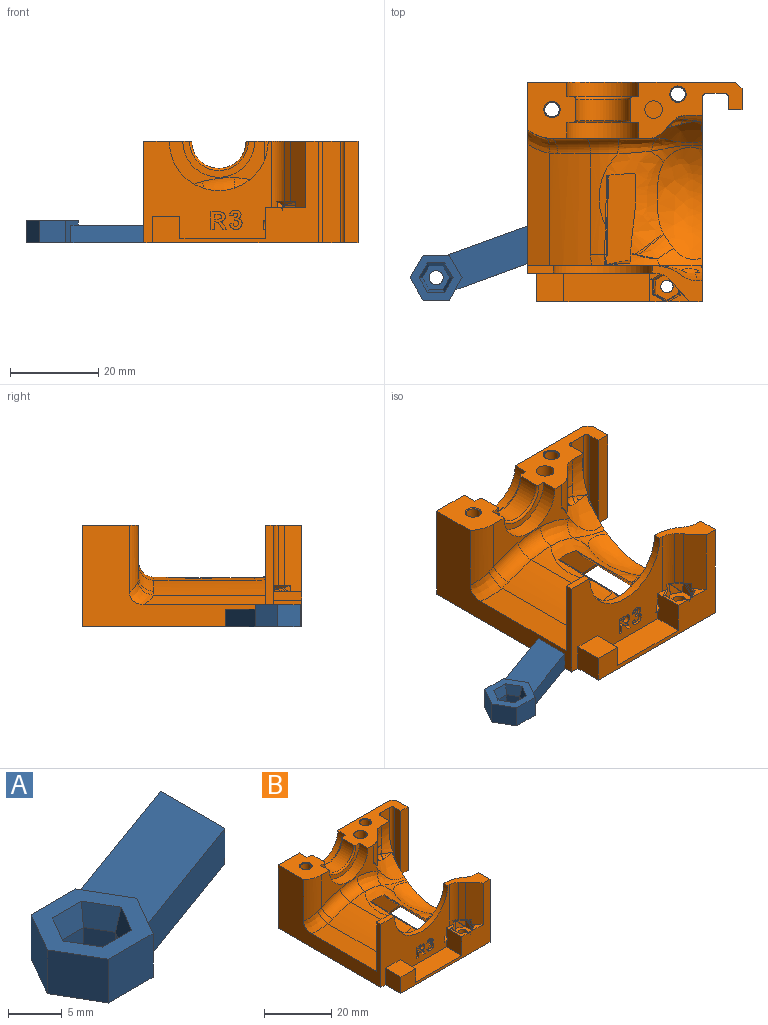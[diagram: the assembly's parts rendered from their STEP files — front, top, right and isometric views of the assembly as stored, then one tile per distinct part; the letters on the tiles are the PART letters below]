
ASSEMBLY  parts=2 mates=1
PART A: 26 faces, bbox 26.7x16.8x5 mm
  f0: plane 2.68x1.9mm, normal (0.87,-0.5,0), area 5.9mm2, adj f1,f5,f8,f12
  f1: plane 3.1x1.9mm, normal (0,-1,0), area 5.9mm2, adj f0,f2,f7,f12
  f2: plane 2.68x1.9mm, normal (-0.87,-0.5,0), area 5.9mm2, adj f1,f3,f6,f12
  f3: plane 2.68x1.9mm, normal (-0.87,0.5,0), area 5.9mm2, adj f2,f4,f11,f12
  f4: plane 3.1x1.9mm, normal (0,1,0), area 5.9mm2, adj f3,f5,f10,f12
  f5: plane 2.68x1.9mm, normal (0.87,0.5,0), area 5.9mm2, adj f0,f4,f9,f12
  f6: plane 3.33x2.5mm, normal (-0.84,-0.48,0.25), area 9mm2, adj f2,f7,f11,f13
  f7: plane 3.85x2.5mm, normal (0,-0.97,0.25), area 9mm2, adj f1,f6,f8,f13
  f8: plane 3.33x2.5mm, normal (0.84,-0.48,0.25), area 9mm2, adj f0,f7,f9,f13
  f9: plane 3.33x2.5mm, normal (0.84,0.48,0.25), area 9mm2, adj f5,f8,f10,f13
  f10: plane 3.85x2.5mm, normal (0,0.97,0.25), area 9mm2, adj f4,f9,f11,f13
  f11: plane 3.33x2.5mm, normal (-0.84,0.48,0.25), area 9mm2, adj f3,f6,f10,f13
  f12: plane 6.2x5.37mm, normal (0,0,1), area 16.9mm2, adj f0,f1,f2,f3,f4,f5,f17
  f13: plane 11.8x10.22mm, normal (0,0,1), area 51.9mm2, adj f6,f7,f8,f9,f10,f11,f14,f15
  f14: plane 5.11x5mm, normal (-0.87,0.5,0), area 29.5mm2, adj f13,f15,f19,f24
  f15: plane 5.11x5mm, normal (-0.87,-0.5,0), area 29.5mm2, adj f13,f14,f16,f24
  f16: plane 5.9x5mm, normal (0,-1,0), area 29.5mm2, adj f13,f15,f20,f24
  f17: cylinder r=1.6mm len=3.2mm, axis (0,0,1), area 6mm2, adj f12,f24
  f18: plane 5.11x2.95mm, normal (0.87,0.5,0), area 5.9mm2, adj f13,f19,f20,f21
  f19: plane 5.9x5mm, normal (0,1,0), area 28.3mm2, adj f13,f14,f18,f21,f23,f24
  f20: plane 5.11x5mm, normal (0.87,-0.5,0), area 16.5mm2, adj f13,f16,f18,f21,f22,f24
  f21: plane 18.11x14.51mm, normal (0,0,1), area 137.7mm2, adj f18,f19,f20,f22,f23,f25
  f22: plane 16.47x6mm, normal (0.34,-0.94,0), area 70.1mm2, adj f20,f21,f24,f25
  f23: plane 18.11x6.59mm, normal (-0.34,0.94,0), area 77.1mm2, adj f19,f21,f24,f25
  f24: plane 26.65x16.81mm, normal (0,0,-1), area 220.1mm2, adj f14,f15,f16,f17,f19,f20,f22,f23
  f25: plane 8.51x4mm, normal (1,0,0), area 34.1mm2, adj f21,f22,f23,f24
PART B: 269 faces, bbox 50.7x51.1x25 mm
  f0: cone r=2.1mm half-angle=24.2deg, axis (0,0,-1), area 12.9mm2, adj f212,f229
  f1: cylinder r=3.1mm len=6.2mm, axis (0,0,-1), area 91.2mm2, adj f127,f129,f208,f209,f210,f211,f229
  f2: cylinder r=2mm len=9.54mm, axis (1,0.06,0), area 24.3mm2, adj f206,f207,f227,f228,f229
  f3: cone r=1.66mm half-angle=13.1deg, axis (0,0,-1), area 11.1mm2, adj f5,f229
  f4: cylinder r=3.1mm len=8mm, axis (0,0,1), area 76.4mm2, adj f105,f191,f192,f193,f194,f229
  f5: cylinder r=1.4mm len=4.71mm, axis (0,0,1), area 41.4mm2, adj f3,f121
  f6: cylinder r=8.15mm len=16.3mm, axis (0,-1,0), area 85.8mm2, adj f109,f195,f199,f224
  f7: cone r=1.6mm half-angle=45deg, axis (1,0,0), area 2.7mm2, adj f14,f216
  f8: cone r=1.6mm half-angle=45deg, axis (1,0,0), area 2.7mm2, adj f15,f216
  f9: cone r=1.85mm half-angle=45deg, axis (0,0,1), area 3.1mm2, adj f16,f199
  f10: cylinder r=8.15mm len=16.3mm, axis (0,-1,0), area 92.2mm2, adj f63,f114,f195,f199
  f11: cylinder r=6.15mm len=12.3mm, axis (0,-1,0), area 92.7mm2, adj f61,f62,f195,f199
  f12: cone r=1.85mm half-angle=45deg, axis (0,0,1), area 3.1mm2, adj f18,f195
  f13: cylinder r=2mm len=4mm, axis (0,0,1), area 50.3mm2, adj f59,f195
  f14: cylinder r=1.4mm len=12.3mm, axis (1,0,0), area 108.2mm2, adj f7,f57
  f15: cylinder r=1.4mm len=12.3mm, axis (1,0,0), area 106.9mm2, adj f8,f144,f182,f213
  f16: cylinder r=1.65mm len=17.3mm, axis (0,0,1), area 179.4mm2, adj f9,f83
  f17: cylinder r=1.65mm len=11.9mm, axis (0,0,1), area 123.4mm2, adj f28,f113
  f18: cylinder r=1.65mm len=14.3mm, axis (0,0,1), area 148.3mm2, adj f12,f58
  f19: plane 1.92x0.27mm, normal (0.04,-1,0), area 0.2mm2, adj f20,f21,f22,f25,f96
  f20: plane 0.08x0mm, normal (0,0,1), area 0mm2, adj f19,f25
  f21: plane 1.07x0.04mm, normal (-0.31,0.95,0), area 0mm2, adj f19,f22,f25
  f22: plane 0.91x0.27mm, normal (-0.52,0.84,-0.15), area 0mm2, adj f19,f21,f25
  f23: plane 1.69x0.97mm, normal (0,-1,0), area 1.5mm2, adj f37,f38,f39,f40,f41,f42
  f24: plane 1.79x0.78mm, normal (-1,0.01,0.06), area 0.6mm2, adj f36,f47,f48,f121
  f25: plane 2.08x0.62mm, normal (0,1,0), area 0.3mm2, adj f19,f20,f21,f22,f26,f50,f52,f94
  f26: plane 0.03x0.02mm, normal (0.49,-0.86,0.16), area 0mm2, adj f25,f50,f52
  f27: plane 4.08x3.33mm, normal (-0.18,-0.29,-0.94), area 3.6mm2, adj f34,f35,f43,f48,f53,f85,f86,f90
  f28: plane 3.3x3.3mm, normal (0,0,-1), area 8.6mm2, adj f17
  f29: plane 2.07x1.78mm, normal (-0.58,0.14,0.8), area 0.1mm2, adj f31,f51,f70,f121
  f30: plane 1.76x0.2mm, normal (0.62,0.78,0.09), area 0.2mm2, adj f45,f46,f70,f74
  f31: plane 2.45x1.78mm, normal (0.49,0.86,0.15), area 2.5mm2, adj f29,f51,f71
  f32: plane 2.66x0.44mm, normal (-0.13,-0.98,0.17), area 0mm2, adj f43,f72,f85
  f33: plane 2.67x2.57mm, normal (-0.34,-0.9,0.27), area 0.3mm2, adj f35,f72,f121
  f34: plane 3.23x2.92mm, normal (-1,0.01,0.04), area 1.4mm2, adj f27,f48,f73
  f35: plane 2.74x2.67mm, normal (-0.52,-0.85,0.06), area 4.3mm2, adj f27,f33,f73,f121
  f36: plane 1.69x0.17mm, normal (0.04,1,0.07), area 0.1mm2, adj f24,f46,f47,f74,f121
  f37: plane 0.65x0.2mm, normal (0,0,1), area 0.1mm2, adj f23,f38,f42,f84
  f38: extruded ~0.61x0.2mm, area 0.1mm2, adj f23,f37,f39,f84
  f39: extruded ~0.46x0.43mm, area 0.1mm2, adj f23,f38,f40,f84
  f40: extruded ~1.07x0.5mm, area 0.3mm2, adj f23,f39,f41,f84
  f41: plane 0.62x0.2mm, normal (0,0,-1), area 0.1mm2, adj f23,f40,f42,f84
  f42: plane 0.97x0.2mm, normal (-1,0,0), area 0.2mm2, adj f23,f37,f41,f84
  f43: plane 2.26x0.4mm, normal (-0.15,-0.97,0.17), area 0.2mm2, adj f27,f32,f85
  f44: plane 3.3x1.76mm, normal (0.97,0,0.24), area 3mm2, adj f49,f71,f85
  f45: plane 0.23x0.2mm, normal (0.59,0.81,0.04), area 0mm2, adj f30,f46,f51,f88
  f46: plane 2.96x1.71mm, normal (-0.45,0.78,0.42), area 0.6mm2, adj f30,f36,f45,f47,f74,f88,f89
  f47: plane 0.88x0.17mm, normal (-1,0.03,0), area 0.1mm2, adj f24,f36,f46,f89,f92
  f48: plane 2.98x2.47mm, normal (-1,-0.03,0.08), area 1.4mm2, adj f24,f27,f34,f93,f121
  f49: plane 3.35x0.16mm, normal (0.87,0,0.49), area 0.6mm2, adj f44,f51,f52,f85,f94,f96
  f50: plane 0.02x0.01mm, normal (0.5,-0.87,0), area 0mm2, adj f25,f26,f52,f94
  f51: plane 3.02x1.79mm, normal (0.44,0.77,0.47), area 0.6mm2, adj f29,f31,f45,f49,f70,f88,f95,f176
  f52: plane 0.18x0.11mm, normal (-0.31,0.95,0), area 0mm2, adj f25,f26,f49,f50,f94,f96
  f53: plane 1.89x1.72mm, normal (-0.5,-0.5,-0.71), area 1.6mm2, adj f27,f86,f90,f100
  f54: bspline ~2.94x2.24mm, area 5.2mm2, adj f55,f102,f103,f104
  f55: cylinder r=2mm len=1.72mm, axis (0.69,0.69,-0.2), area 1.3mm2, adj f54,f104,f111
  f56: bspline ~11.68x7.37mm, area 25.4mm2, adj f76,f97,f104,f114,f216
  f57: plane 2.8x2.8mm, normal (1,0,0), area 6.2mm2, adj f14
  f58: plane 3.4x3.4mm, normal (0,0,-1), area 3mm2, adj f18,f105,f106,f107,f108
  f59: plane 4x4mm, normal (0,0,1), area 12.6mm2, adj f13
  f60: bspline ~6.13x0.26mm, area 1.3mm2, adj f111,f112,f195
  f61: torus R=6.65mm, axis (0,1,0), area 15.6mm2, adj f11,f109,f195,f199
  f62: torus R=6.65mm, axis (0,1,0), area 15.6mm2, adj f11,f63,f195,f199
  f63: plane 16.3x8.15mm, normal (0,-1,0), area 34.9mm2, adj f10,f62,f195,f199
  f64: torus R=26mm, axis (0,-1,0), area 36.6mm2, adj f69,f76,f79,f114
  f65: bspline ~1.24x0.63mm, area 0.2mm2, adj f66,f104,f110,f114
  f66: bspline ~0.61x0.55mm, area 0.1mm2, adj f65,f67,f110,f114
  f67: bspline ~0.36x0.31mm, area 0mm2, adj f66,f110,f114
  f68: bspline ~4.1x2.33mm, area 5.6mm2, adj f99,f101,f117,f120
  f69: torus R=63.5mm, axis (0,-1,0), area 43.8mm2, adj f64,f114,f115,f118
  f70: plane 2.37x1.81mm, normal (0.55,0.83,0.09), area 2.7mm2, adj f29,f30,f51,f74,f121
  f71: plane 3.21x1.78mm, normal (0.98,-0.02,0.21), area 2.8mm2, adj f31,f44,f121
  f72: plane 2.67x2.45mm, normal (-0.45,-0.88,0.16), area 3.7mm2, adj f32,f33,f121
  f73: plane 3.23x2.69mm, normal (-1,0,0.06), area 4.2mm2, adj f34,f35,f121
  f74: plane 2.86x1.77mm, normal (-0.5,0.86,0.09), area 5.1mm2, adj f30,f36,f46,f70,f121
  f75: bspline ~6.61x4.95mm, area 3.4mm2, adj f98,f123,f124,f184
  f76: bspline ~9.15x5.42mm, area 44.1mm2, adj f56,f64,f114,f123
  f77: bspline ~1.82x0.84mm, area 0.7mm2, adj f80,f124,f125,f126,f206,f207
  f78: cylinder r=2.5mm len=4.4mm, axis (-0.98,0,0.22), area 0mm2, adj f98,f124
  f79: cylinder r=22.5mm len=22.8mm, axis (0,-1,0), area 71mm2, adj f64,f81,f118,f123,f124
  f80: bspline ~2.43x0.46mm, area 0.8mm2, adj f77,f81,f124,f126
  f81: cylinder r=0.51mm len=6.75mm, axis (-0.02,-1,0), area 2.4mm2, adj f79,f80,f82,f126
  f82: bspline ~11.28x0.6mm, area 4.4mm2, adj f81,f123,f126,f205
  f83: plane 3.4x3.4mm, normal (0,0,-1), area 3mm2, adj f16,f127,f128,f129,f130
  f84: plane 4.21x3.74mm, normal (0,-1,0), area 8.2mm2, adj f37,f38,f39,f40,f41,f42,f132,f133
  f85: plane 3.65x3.01mm, normal (0.49,-0.86,0.16), area 7.1mm2, adj f27,f32,f43,f44,f49,f86,f96,f121
  f86: cone r=4.8mm half-angle=45deg, axis (0,0,-1), area 1.8mm2, adj f27,f53,f85,f145
  f87: plane 4.44x2.91mm, normal (0,-1,0), area 6.2mm2, adj f148,f149,f150,f151,f152,f153,f154,f155
  f88: plane 0.28x0.2mm, normal (0.57,0.82,0), area 0mm2, adj f45,f46,f51,f89,f176
  f89: plane 3.1x1.8mm, normal (-0.35,0.61,0.71), area 1.6mm2, adj f46,f47,f88,f91,f92,f176,f177,f215
  f90: plane 1.63x1.16mm, normal (-0.53,-0.46,-0.71), area 0.7mm2, adj f27,f53,f93,f178
  f91: plane 1.04x0.15mm, normal (-0.71,0.02,0.71), area 0.2mm2, adj f89,f92,f177,f178
  f92: plane 1.04x0.17mm, normal (-0.92,0.03,0.38), area 0.2mm2, adj f47,f89,f91,f178
  f93: plane 1.8x1.64mm, normal (-1,0.03,0), area 1.4mm2, adj f27,f48,f90,f178
  f94: plane 3.41x0.16mm, normal (0.65,0,0.76), area 0.7mm2, adj f25,f49,f50,f52,f95,f183
  f95: plane 3.17x1.74mm, normal (0.33,0.57,0.75), area 0.7mm2, adj f51,f94,f176,f183,f215
  f96: plane 2.63x1.28mm, normal (0.33,-0.57,0.75), area 1.1mm2, adj f19,f25,f49,f52,f85,f145,f183
  f97: bspline ~13.04x7.69mm, area 16.4mm2, adj f56,f123,f184,f216
  f98: bspline ~8.1x5.63mm, area 25.2mm2, adj f75,f78,f184,f185
  f99: bspline ~1.45x0.89mm, area 0.4mm2, adj f68,f117,f186
  f100: plane 13.6x1.39mm, normal (-0.71,-0.71,0), area 26.8mm2, adj f53,f145,f178,f187
  f101: bspline ~12.76x4.01mm, area 43.9mm2, adj f68,f119,f120,f186,f187
  f102: bspline ~4.24x2.24mm, area 3.4mm2, adj f54,f104,f188
  f103: bspline ~3.58x3.49mm, area 8.2mm2, adj f54,f111,f112,f188
  f104: bspline ~12.95x11.5mm, area 65.8mm2, adj f54,f55,f56,f65,f102,f110,f111,f114
  f105: plane 5.18x1mm, normal (0,1,0), area 4.3mm2, adj f4,f58,f106,f108,f192,f194
  f106: plane 3.4x0.5mm, normal (1,0,0), area 1.7mm2, adj f58,f105,f107,f194
  f107: plane 3.4x0.5mm, normal (0,-1,0), area 1.7mm2, adj f58,f106,f108,f194
  f108: plane 3.4x0.5mm, normal (-1,0,0), area 1.7mm2, adj f58,f105,f107,f194
  f109: plane 16.3x8.15mm, normal (0,1,0), area 34.9mm2, adj f6,f61,f195,f199
  f110: cylinder r=4mm len=9.21mm, axis (0,0,-1), area 25.5mm2, adj f65,f66,f67,f104,f111,f114,f195
  f111: plane 9.46x3.1mm, normal (0.71,-0.71,0), area 32.6mm2, adj f55,f60,f103,f104,f110,f195
  f112: bspline ~7.75x3.2mm, area 23mm2, adj f60,f103,f188,f195
  f113: plane 8.07x5.6mm, normal (0,0,-1), area 36.6mm2, adj f17,f131,f196,f197,f198
  f114: plane 24.79x12.05mm, normal (0,-1,0), area 101.7mm2, adj f10,f56,f64,f65,f66,f67,f69,f76
  f115: bspline ~4.07x3.62mm, area 9.7mm2, adj f69,f118,f200,f201
  f116: bspline ~3x1.94mm, area 0.5mm2, adj f117,f120,f203
  f117: bspline ~7.8x6.44mm, area 11.3mm2, adj f68,f99,f116,f120,f186,f203
  f118: cylinder r=60mm len=25.48mm, axis (0,-1,0), area 251.1mm2, adj f69,f79,f115,f124,f202,f203
  f119: bspline ~6.44x3.62mm, area 18.2mm2, adj f101,f120,f187,f203
  f120: bspline ~11.41x6.88mm, area 50.4mm2, adj f68,f101,f116,f117,f119,f203
  f121: plane 6.47x5.63mm, normal (0,-0.01,1), area 17.6mm2, adj f5,f24,f29,f33,f35,f36,f48,f70
  f122: cylinder r=22.5mm len=0.85mm, axis (0,-1,0), area 0.2mm2, adj f123,f124,f204
  f123: bspline ~26.1x14.86mm, area 184.3mm2, adj f75,f76,f79,f82,f97,f122,f184,f204
  f124: bspline ~16.74x11mm, area 23mm2, adj f75,f77,f78,f79,f80,f118,f122,f125
  f125: bspline ~1.93x0.86mm, area 0.5mm2, adj f77,f124,f206
  f126: cylinder r=1.01mm len=20.37mm, axis (-0.02,-1,0), area 3.7mm2, adj f77,f80,f81,f82,f205,f207
  f127: plane 5.18x1mm, normal (0,-1,0), area 4.3mm2, adj f1,f83,f128,f130,f208,f209,f211
  f128: plane 3.4x0.5mm, normal (-1,0,0), area 1.7mm2, adj f83,f127,f129,f209
  f129: plane 5.18x1mm, normal (0,1,0), area 4.3mm2, adj f1,f83,f128,f130,f209,f210,f211
  f130: plane 3.4x0.5mm, normal (1,0,0), area 1.7mm2, adj f83,f127,f129,f211
  f131: plane 5.6x2.1mm, normal (0,1,0), area 11.8mm2, adj f113,f196,f198,f212
  f132: plane 1.2x0.77mm, normal (0,0,1), area 0.9mm2, adj f84,f133,f143,f213
  f133: plane 4x1.2mm, normal (1,0,0), area 4.8mm2, adj f84,f132,f134,f213
  f134: plane 1.68x1.2mm, normal (0,0,-1), area 2mm2, adj f84,f133,f135,f213
  f135: extruded ~1.55x1.2mm, area 2.6mm2, adj f84,f134,f136,f213
  f136: extruded ~1.2x1.1mm, area 2mm2, adj f84,f135,f137,f213
  f137: extruded ~1.2x1mm, area 1.6mm2, adj f84,f136,f138,f213
  f138: plane 1.2x0.79mm, normal (-0.85,0,-0.52), area 1.1mm2, adj f84,f137,f139,f213
  f139: plane 1.2x0.9mm, normal (0,0,1), area 1.1mm2, adj f84,f138,f140,f213
  f140: plane 1.2x0.91mm, normal (0.85,0,0.53), area 1.3mm2, adj f84,f139,f141,f213
  f141: extruded ~1.2x1.13mm, area 1.8mm2, adj f84,f140,f142,f213
  f142: plane 1.2x0.17mm, normal (0,0,1), area 0.2mm2, adj f84,f141,f143,f213
  f143: plane 1.69x1.2mm, normal (-1,0,0), area 2mm2, adj f84,f132,f142,f213
  f144: plane 2.8x2.4mm, normal (1,0,0), area 5.6mm2, adj f15,f213
  f145: cylinder r=4mm len=15.4mm, axis (0,0,1), area 44.8mm2, adj f85,f86,f96,f100,f183,f187,f213
  f146: cylinder r=11.2mm len=22.4mm, axis (0,1,0), area 59.8mm2, adj f147,f187,f203,f213
  f147: plane 5.78x1.7mm, normal (0,0,1), area 9.8mm2, adj f146,f203,f213,f225
  f148: extruded ~0.97x0.8mm, area 0.8mm2, adj f87,f149,f175,f213
  f149: extruded ~0.87x0.8mm, area 0.8mm2, adj f87,f148,f150,f213
  f150: plane 0.8x0.8mm, normal (0.14,0,-0.99), area 0.6mm2, adj f87,f149,f151,f213
  f151: extruded ~0.8x0.46mm, area 0.4mm2, adj f87,f150,f152,f213
  f152: extruded ~0.8x0.41mm, area 0.4mm2, adj f87,f151,f153,f213
  f153: extruded ~0.8x0.43mm, area 0.4mm2, adj f87,f152,f154,f213
  f154: extruded ~0.8x0.52mm, area 0.4mm2, adj f87,f153,f155,f213
  f155: extruded ~0.8x0.49mm, area 0.4mm2, adj f87,f154,f156,f213
  f156: extruded ~0.8x0.41mm, area 0.4mm2, adj f87,f155,f157,f213
  f157: extruded ~0.8x0.38mm, area 0.3mm2, adj f87,f156,f158,f213
  f158: plane 0.8x0.67mm, normal (0.99,0,-0.12), area 0.5mm2, adj f87,f157,f159,f213
  f159: extruded ~0.8x0.51mm, area 0.4mm2, adj f87,f158,f160,f213
  f160: extruded ~0.8x0.41mm, area 0.4mm2, adj f87,f159,f161,f213
  f161: extruded ~0.8x0.34mm, area 0.3mm2, adj f87,f160,f162,f213
  f162: extruded ~0.8x0.35mm, area 0.3mm2, adj f87,f161,f163,f213
  f163: extruded ~0.8x0.36mm, area 0.3mm2, adj f87,f162,f164,f213
  f164: extruded ~0.8x0.43mm, area 0.4mm2, adj f87,f163,f165,f213
  f165: plane 0.8x0.76mm, normal (0.15,0,0.99), area 0.6mm2, adj f87,f164,f166,f213
  f166: extruded ~0.8x0.63mm, area 0.5mm2, adj f87,f165,f167,f213
  f167: extruded ~0.8x0.44mm, area 0.5mm2, adj f87,f166,f168,f213
  f168: extruded ~0.8x0.64mm, area 0.5mm2, adj f87,f167,f169,f213
  f169: extruded ~0.98x0.8mm, area 0.9mm2, adj f87,f168,f170,f213
  f170: extruded ~0.8x0.71mm, area 0.6mm2, adj f87,f169,f171,f213
  f171: extruded ~0.91x0.8mm, area 0.9mm2, adj f87,f170,f172,f213
  f172: extruded ~0.8x0.6mm, area 0.6mm2, adj f87,f171,f173,f213
  f173: extruded ~0.8x0.66mm, area 0.6mm2, adj f87,f172,f174,f213
  f174: extruded ~0.97x0.8mm, area 0.9mm2, adj f87,f173,f175,f213
  f175: extruded ~1.02x0.8mm, area 0.9mm2, adj f87,f148,f174,f213
  f176: plane 0.1x0.04mm, normal (1,0,0), area 0mm2, adj f51,f88,f89,f95,f215
  f177: plane 4.7x2.39mm, normal (0,0,1), area 4.5mm2, adj f89,f91,f178,f215
  f178: plane 15.4x3.93mm, normal (-0.75,-0.66,0), area 76.2mm2, adj f90,f91,f92,f93,f100,f177,f187,f215
  f179: plane 6.5x6.2mm, normal (0,0,1), area 40.3mm2, adj f180,f213,f214,f215
  f180: plane 6.5x5mm, normal (1,0,0), area 32.5mm2, adj f179,f181,f213,f215
  f181: plane 19.4x6.5mm, normal (0,0,1), area 126.1mm2, adj f180,f182,f213,f215
  f182: plane 6.9x6.5mm, normal (-1,0,0), area 44.3mm2, adj f15,f181,f183,f213,f215
  f183: plane 6.5x3.6mm, normal (0,0,1), area 8.1mm2, adj f25,f94,f95,f96,f145,f182,f213,f215
  f184: bspline ~27.19x11.69mm, area 263.2mm2, adj f75,f97,f98,f123,f185,f216
  f185: bspline ~12.99x8.59mm, area 29.5mm2, adj f98,f124,f184,f203,f216
  f186: cylinder r=19mm len=14.27mm, axis (1,0,0), area 14.5mm2, adj f99,f101,f117,f187,f203,f216
  f187: plane 11.46x8.34mm, normal (0,0,1), area 38.2mm2, adj f100,f101,f119,f145,f146,f178,f186,f203
  f188: cylinder r=19mm len=15.44mm, axis (1,0,0), area 39.4mm2, adj f102,f103,f104,f112,f195,f216
  f189: cylinder r=1mm len=23mm, axis (0,0,-1), area 36.1mm2, adj f195,f216,f217,f229
  f190: cylinder r=1mm len=23mm, axis (0,0,-1), area 36.1mm2, adj f195,f217,f218,f229
  f191: plane 8x0mm, normal (0,1,0), area 0mm2, adj f4,f194,f222,f229
  f192: plane 5.18x1.4mm, normal (0,0,-1), area 5.1mm2, adj f4,f105
  f193: plane 8x0mm, normal (0,1,0), area 0mm2, adj f4,f194,f223,f229
  f194: plane 6.2x4.45mm, normal (0,0,-1), area 15.5mm2, adj f4,f105,f106,f107,f108,f191,f193,f222
  f195: plane 25.53x12.93mm, normal (0,0,1), area 163.2mm2, adj f6,f10,f11,f12,f13,f60,f61,f62
  f196: plane 9.75x3.78mm, normal (-1,0,0), area 21.9mm2, adj f113,f131,f197,f212,f224
  f197: plane 5.6x1.68mm, normal (0,0.71,-0.71), area 13.3mm2, adj f113,f196,f198,f224
  f198: plane 9.75x3.78mm, normal (1,0,0), area 21.9mm2, adj f113,f131,f197,f212,f224
  f199: plane 12.75x10.85mm, normal (0,0,1), area 110.1mm2, adj f6,f9,f10,f11,f61,f62,f63,f109
  f200: cylinder r=8.5mm len=15.18mm, axis (0,0,1), area 80.2mm2, adj f114,f115,f199,f201,f225
  f201: bspline ~6.05x5.87mm, area 26.2mm2, adj f115,f200,f202,f225
  f202: plane 27.5x4.88mm, normal (-0.41,0,0.91), area 140.5mm2, adj f118,f201,f203,f225
  f203: plane 39.67x18.17mm, normal (0,1,0), area 201.4mm2, adj f116,f117,f118,f119,f120,f124,f146,f147
  f204: plane 20.54x1.95mm, normal (-0.81,0.02,-0.59), area 27.2mm2, adj f122,f123,f124,f205,f206,f227
  f205: plane 14.97x9.48mm, normal (0.06,-0.99,-0.11), area 48.7mm2, adj f82,f123,f126,f204,f207,f226,f227
  f206: plane 13.73x9.2mm, normal (-0.06,0.99,0.11), area 46.8mm2, adj f2,f77,f124,f125,f204,f207,f227
  f207: plane 22.25x10.17mm, normal (0.74,-0.02,0.67), area 274.5mm2, adj f2,f77,f126,f205,f206,f226,f228
  f208: plane 5.18x1.4mm, normal (0,0,-1), area 5.1mm2, adj f1,f127
  f209: plane 3.4x1.4mm, normal (0,0,-1), area 4.2mm2, adj f1,f127,f128,f129
  f210: plane 5.18x1.4mm, normal (0,0,-1), area 5.1mm2, adj f1,f129
  f211: plane 3.4x1.4mm, normal (0,0,-1), area 4.2mm2, adj f1,f127,f129,f130
  f212: plane 9.75x5.6mm, normal (0,0,1), area 46mm2, adj f0,f131,f196,f198,f224
  f213: plane 28.96x23.03mm, normal (0,-1,0), area 384.1mm2, adj f15,f132,f133,f134,f135,f136,f137,f138
  f214: plane 6.5x6mm, normal (-1,0,0), area 39mm2, adj f179,f213,f215,f229
  f215: plane 37.5x23mm, normal (0,-1,0), area 194.6mm2, adj f89,f95,f176,f177,f178,f179,f180,f181
  f216: plane 46.45x23.25mm, normal (1,0,0), area 365.8mm2, adj f7,f8,f56,f97,f104,f184,f185,f186
  f217: plane 23x4mm, normal (0,-1,0), area 92mm2, adj f189,f190,f195,f229
  f218: plane 23x2.7mm, normal (-1,0,0), area 62.1mm2, adj f190,f195,f219,f229
  f219: plane 23x3mm, normal (0,-1,0), area 69mm2, adj f195,f218,f220,f229
  f220: plane 23x4.83mm, normal (1,0,0), area 111.1mm2, adj f195,f219,f221,f229
  f221: plane 23x1.42mm, normal (0.71,0.71,0), area 46.2mm2, adj f195,f220,f224,f229
  f222: plane 8x2.65mm, normal (-1,0,0), area 21.2mm2, adj f191,f194,f224,f229
  f223: plane 8x2.65mm, normal (1,0,0), area 21.2mm2, adj f193,f194,f224,f229
  f224: plane 47.08x23mm, normal (0,1,0), area 907.7mm2, adj f6,f194,f195,f196,f197,f198,f199,f212
  f225: plane 44.34x24.09mm, normal (-1,0,0), area 442.3mm2, adj f147,f199,f200,f201,f202,f203,f213,f224
  f226: cylinder r=2mm len=9.45mm, axis (-1,-0.06,0), area 20.8mm2, adj f205,f207,f227,f228,f229
  f227: cylinder r=31mm len=24.49mm, axis (0.02,1,0), area 292.8mm2, adj f2,f204,f205,f206,f226,f229
  f228: cylinder r=0.5mm len=24.27mm, axis (0.02,1,0), area 26.1mm2, adj f2,f207,f226,f229
  f229: plane 49.75x48.5mm, normal (0,0,-1), area 1690.1mm2, adj f0,f1,f2,f3,f4,f189,f190,f191
  f230: cylinder r=0.5mm len=1.24mm, axis (-0.41,0,0.91), area 2.5mm2, adj f231,f232
  f231: plane 1x0.91mm, normal (0.41,0,-0.91), area 0.8mm2, adj f230
  f232: plane 1x0.91mm, normal (-0.41,0,0.91), area 0.8mm2, adj f230
  f233: cylinder r=0.5mm len=1.24mm, axis (-0.41,0,0.91), area 2.5mm2, adj f234,f235
  f234: plane 1x0.91mm, normal (0.41,0,-0.91), area 0.8mm2, adj f233
  f235: plane 1x0.91mm, normal (-0.41,0,0.91), area 0.8mm2, adj f233
  f236: cylinder r=0.5mm len=1.24mm, axis (-0.41,0,0.91), area 2.5mm2, adj f237,f238
  f237: plane 1x0.91mm, normal (0.41,0,-0.91), area 0.8mm2, adj f236
  f238: plane 1x0.91mm, normal (-0.41,0,0.91), area 0.8mm2, adj f236
  f239: cylinder r=0.5mm len=1.24mm, axis (-0.41,0,0.91), area 2.5mm2, adj f240,f241
  f240: plane 1x0.91mm, normal (0.41,0,-0.91), area 0.8mm2, adj f239
  f241: plane 1x0.91mm, normal (-0.41,0,0.91), area 0.8mm2, adj f239
  f242: cylinder r=0.5mm len=1.24mm, axis (-0.41,0,0.91), area 2.5mm2, adj f243,f244
  f243: plane 1x0.91mm, normal (0.41,0,-0.91), area 0.8mm2, adj f242
  f244: plane 1x0.91mm, normal (-0.41,0,0.91), area 0.8mm2, adj f242
  f245: cylinder r=0.5mm len=1.24mm, axis (-0.41,0,0.91), area 2.5mm2, adj f246,f247
  f246: plane 1x0.91mm, normal (0.41,0,-0.91), area 0.8mm2, adj f245
  f247: plane 1x0.91mm, normal (-0.41,0,0.91), area 0.8mm2, adj f245
  f248: cylinder r=0.5mm len=1.24mm, axis (-0.41,0,0.91), area 2.5mm2, adj f249,f250
  f249: plane 1x0.91mm, normal (0.41,0,-0.91), area 0.8mm2, adj f248
  f250: plane 1x0.91mm, normal (-0.41,0,0.91), area 0.8mm2, adj f248
  f251: cylinder r=0.5mm len=1.24mm, axis (-0.41,0,0.91), area 2.5mm2, adj f252,f253
  f252: plane 1x0.91mm, normal (0.41,0,-0.91), area 0.8mm2, adj f251
  f253: plane 1x0.91mm, normal (-0.41,0,0.91), area 0.8mm2, adj f251
  f254: cylinder r=0.5mm len=1.24mm, axis (-0.41,0,0.91), area 2.5mm2, adj f255,f256
  f255: plane 1x0.91mm, normal (0.41,0,-0.91), area 0.8mm2, adj f254
  f256: plane 1x0.91mm, normal (-0.41,0,0.91), area 0.8mm2, adj f254
  f257: cylinder r=0.5mm len=1.24mm, axis (-0.41,0,0.91), area 2.5mm2, adj f258,f259
  f258: plane 1x0.91mm, normal (0.41,0,-0.91), area 0.8mm2, adj f257
  f259: plane 1x0.91mm, normal (-0.41,0,0.91), area 0.8mm2, adj f257
  f260: cylinder r=0.5mm len=1.24mm, axis (-0.41,0,0.91), area 2.5mm2, adj f261,f262
  f261: plane 1x0.91mm, normal (0.41,0,-0.91), area 0.8mm2, adj f260
  f262: plane 1x0.91mm, normal (-0.41,0,0.91), area 0.8mm2, adj f260
  f263: cylinder r=0.5mm len=1.24mm, axis (-0.41,0,0.91), area 2.5mm2, adj f264,f265
  f264: plane 1x0.91mm, normal (0.41,0,-0.91), area 0.8mm2, adj f263
  f265: plane 1x0.91mm, normal (-0.41,0,0.91), area 0.8mm2, adj f263
  f266: cylinder r=0.5mm len=1.24mm, axis (-0.41,0,0.91), area 2.5mm2, adj f267,f268
  f267: plane 1x0.91mm, normal (0.41,0,-0.91), area 0.8mm2, adj f266
  f268: plane 1x0.91mm, normal (-0.41,0,0.91), area 0.8mm2, adj f266
PLACE A t=(2.36,9,4.76)mm
PLACE B t=(2.36,9,4.76)mm
MATE fastened A.f24 <-> B.f3  axis (0,0,-1) through (16.86,-31.5,-35.24)mm
